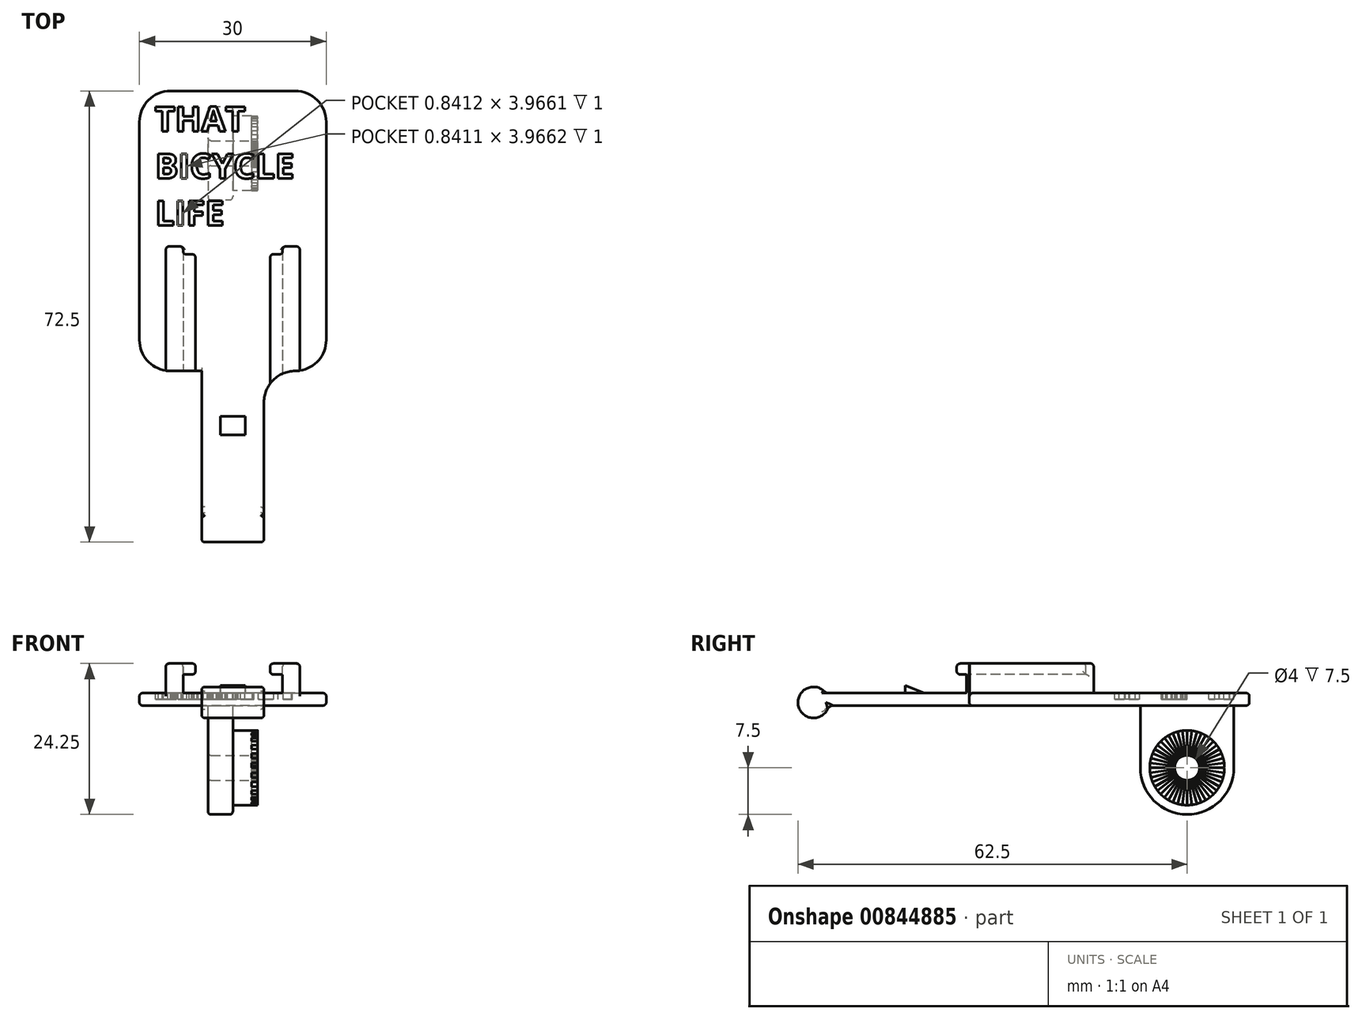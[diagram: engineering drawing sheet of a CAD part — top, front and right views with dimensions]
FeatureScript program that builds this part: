
annotation { "Feature Type Name" : "Feature", "Feature Type Description" : "" }
export const myFeature = defineFeature(function(context is Context, id is Id, definition is map)
    precondition{}
    {
        {
            var Q0;
            Q0=qCreatedBy(makeId("Top.planeOp"),FACE);
            var sketch = newSketch(context, id + "F0", { "sketchPlane" : qUnion([Q0])});
            skLineSegment(sketch, "E0.bottom", {"start": v(-15, 25) * mm, "end": v(15, 25) * mm});
            skLineSegment(sketch, "E0.top", {"start": v(-15, -20) * mm, "end": v(15, -20) * mm});
            skLineSegment(sketch, "E0.left", {"start": v(-15, 25) * mm, "end": v(-15, -20) * mm});
            skLineSegment(sketch, "E0.right", {"start": v(15, 25) * mm, "end": v(15, -20) * mm});
            skSolve(sketch);
        }
        {
            var Q0;
            Q0=qSketchRegion(id+"F0",true);
            extrude(context, id + "F1", {"entities" : qUnion([Q0]), "depth" : 2 * mm, "offsetDistance" : 25 * mm});
        }
        {
            var Q0;
            Q0=makeQuery(id+"F1.opExtrude","CAP_FACE",FACE,{"disambiguationData":[OSD([sQuery(id+"F0.wireOp",EDGE,"E0.bottom"),sQuery(id+"F0.wireOp",EDGE,"E0.top"),sQuery(id+"F0.wireOp",EDGE,"E0.left"),sQuery(id+"F0.wireOp",EDGE,"E0.right")])],"isStart":true});
            var sketch = newSketch(context, id + "F2", { "sketchPlane" : qUnion([Q0])});
            skLineSegment(sketch, "E1.bottom", {"start": v(10.75, 20) * mm, "end": v(-10.75, 20) * mm});
            skLineSegment(sketch, "E1.top", {"start": v(10.75, 0) * mm, "end": v(-10.75, 0) * mm});
            skLineSegment(sketch, "E1.left", {"start": v(10.75, 20) * mm, "end": v(10.75, 0) * mm});
            skLineSegment(sketch, "E1.right", {"start": v(-10.75, 20) * mm, "end": v(-10.75, 0) * mm});
            skSolve(sketch);
        }
        {
            var Q0;
            Q0=qSketchRegion(id+"F2",true);
            extrude(context, id + "F3", {"entities" : qUnion([Q0]), "operationType" : NewBodyOperationType.ADD, "depth" : 4.75 * mm, "offsetDistance" : 25 * mm});
        }
        {
            var Q0;
            Q0=makeQuery(id+"F3.boolean.opBoolean","MERGE",FACE,{"derivedFrom":[makeQuery(id+"FSz8aaNzwJ16Nas_1.boolean.opBoolean","MERGE",FACE,{"derivedFrom":[makeQuery(id+"F1.opExtrude","SWEPT_FACE",FACE,{"disambiguationData":[OSD([sQuery(id+"F0.wireOp",EDGE,"E0.top")])]}),makeQuery(id+"FSz8aaNzwJ16Nas_1.opExtrude","SWEPT_FACE",FACE,{"disambiguationData":[OSD([sQuery(id+"FtYRrhxxuHg0Pyv_1.wireOp",EDGE,"OmNEySeM-kDo9-KMJ4-0k0w-oykvhkZkCSKl.top")])]})]}),makeQuery(id+"F3.opExtrude","SWEPT_FACE",FACE,{"disambiguationData":[OSD([sQuery(id+"F2.wireOp",EDGE,"E1.bottom")])]})]});
            var sketch = newSketch(context, id + "F4", { "sketchPlane" : qUnion([Q0])});
            skLineSegment(sketch, "E2", {"start": v(-6, -4.75) * mm, "end": v(-6, -3) * mm});
            skLineSegment(sketch, "E3", {"start": v(-6, -3) * mm, "end": v(-8, -3) * mm});
            skLineSegment(sketch, "E4", {"start": v(-8, -3) * mm, "end": v(-8, 0) * mm});
            skLineSegment(sketch, "E5", {"start": v(-8, 0) * mm, "end": v(8, 0) * mm});
            skLineSegment(sketch, "E6", {"start": v(8, 0) * mm, "end": v(8, -3) * mm});
            skLineSegment(sketch, "E7", {"start": v(8, -3) * mm, "end": v(6, -3) * mm});
            skLineSegment(sketch, "E8", {"start": v(6, -3) * mm, "end": v(6, -4.75) * mm});
            skLineSegment(sketch, "E9", {"start": v(-6, -4.75) * mm, "end": v(6, -4.75) * mm});
            skSolve(sketch);
        }
        {
            var Q0;
            Q0=qSketchRegion(id+"F4",true);
            extrude(context, id + "F5", {"entities" : qUnion([Q0]), "operationType" : NewBodyOperationType.REMOVE, "oppositeDirection" : true, "depth" : 25 * mm, "offsetDistance" : 25 * mm});
        }
        {
            var Q0;
            Q0=qCreatedBy(makeId("Top.planeOp"),FACE);
            var sketch = newSketch(context, id + "F6", { "sketchPlane" : qUnion([Q0])});
            skLineSegment(sketch, "E10.bottom", {"start": v(5, -20) * mm, "end": v(-5, -20) * mm});
            skLineSegment(sketch, "E10.top", {"start": v(5, -45) * mm, "end": v(-5, -45) * mm});
            skLineSegment(sketch, "E10.left", {"start": v(5, -20) * mm, "end": v(5, -45) * mm});
            skLineSegment(sketch, "E10.right", {"start": v(-5, -20) * mm, "end": v(-5, -45) * mm});
            skSolve(sketch);
        }
        {
            var Q0;
            Q0=qSketchRegion(id+"F6",true);
            extrude(context, id + "F7", {"entities" : qUnion([Q0]), "operationType" : NewBodyOperationType.ADD, "depth" : 2 * mm, "offsetDistance" : 25 * mm});
        }
        {
            var Q0;
            Q0=qCreatedBy(makeId("Right.planeOp"),FACE);
            var sketch = newSketch(context, id + "F8", { "sketchPlane" : qUnion([Q0])});
            skLineSegment(sketch, "E11", {"start": v(-27.25, 0) * mm, "end": v(-30.25, -1.25) * mm});
            skLineSegment(sketch, "E12", {"start": v(-30.25, -1.25) * mm, "end": v(-30.25, 0) * mm});
            skLineSegment(sketch, "E13", {"start": v(-30.25, 0) * mm, "end": v(-27.25, 0) * mm});
            skSolve(sketch);
        }
        {
            var Q0;
            Q0=qSketchRegion(id+"F8",true);
            extrude(context, id + "F9", {"entities" : qUnion([Q0]), "operationType" : NewBodyOperationType.ADD, "endBound" : BoundingType.SYMMETRIC, "depth" : 4 * mm, "offsetDistance" : 25 * mm});
        }
        {
            var Q0;
            {var subQ0=sQuery(id+"F2.wireOp",EDGE,"E1.bottom");var subQ1=sQuery(id+"F2.wireOp",EDGE,"E1.top");var subQ2=sQuery(id+"F2.wireOp",EDGE,"E1.left");Q0=makeQuery(id+"F5.boolean.opBoolean","SPLIT",FACE,{"disambiguationData":[TD([makeQuery(id+"F3.opExtrude","SWEPT_FACE",FACE,{"disambiguationData":[OSD([subQ2])]})])],"derivedFrom":makeQuery(id+"F3.opExtrude","CAP_FACE",FACE,{"disambiguationData":[OSD([subQ0,subQ1,subQ2,sQuery(id+"F2.wireOp",EDGE,"E1.right")])],"isStart":false})});}
            var sketch = newSketch(context, id + "F10", { "sketchPlane" : qUnion([Q0])});
            skLineSegment(sketch, "E14.bottom", {"start": v(8, 1.25) * mm, "end": v(-8, 1.25) * mm});
            skLineSegment(sketch, "E14.top", {"start": v(8, -3.75) * mm, "end": v(-8, -3.75) * mm});
            skLineSegment(sketch, "E14.left", {"start": v(8, 1.25) * mm, "end": v(8, -3.75) * mm});
            skLineSegment(sketch, "E14.right", {"start": v(-8, 1.25) * mm, "end": v(-8, -3.75) * mm});
            skSolve(sketch);
        }
        {
            var Q0;
            Q0=qSketchRegion(id+"F10",true);
            extrude(context, id + "F11", {"entities" : qUnion([Q0]), "operationType" : NewBodyOperationType.REMOVE, "oppositeDirection" : true, "depth" : 4.75 * mm, "offsetDistance" : 25 * mm});
        }
        {
            var Q0;
            Q0=qCreatedBy(makeId("Right.planeOp"),FACE);
            var sketch = newSketch(context, id + "F12", { "sketchPlane" : qUnion([Q0])});
            skCircle(sketch, "E15", {"center": v(-45, 1.5) * mm, "radius": 2.5 * mm});
            skSolve(sketch);
        }
        {
            var Q0;
            Q0=qSketchRegion(id+"F12",true);
            extrude(context, id + "F13", {"entities" : qUnion([Q0]), "operationType" : NewBodyOperationType.ADD, "endBound" : BoundingType.SYMMETRIC, "depth" : 10 * mm, "offsetDistance" : 25 * mm});
        }
        {
            var Q0;
            Q0=qCreatedBy(makeId("Right.planeOp"),FACE);
            var sketch = newSketch(context, id + "F14", { "sketchPlane" : qUnion([Q0])});
            skLineSegment(sketch, "E16.0", {"start": v(22.5, 2) * mm, "end": v(7.5, 2) * mm});
            skArc(sketch, "E17", {"start": v(22.5, 12) * mm, "mid": v(15, 19.5) * mm, "end": v(7.5, 12) * mm});
            skLineSegment(sketch, "E18", {"start": v(22.5, 12) * mm, "end": v(22.5, 2) * mm});
            skLineSegment(sketch, "E19", {"start": v(7.5, 12) * mm, "end": v(7.5, 2) * mm});
            skPoint(sketch, "E20.orphan", {"position": v(25, 2) * mm});
            skSolve(sketch);
        }
        {
            var Q0;
            Q0 = qSketchRegion(id + "F14", true);
            extrude(context, id + "F15", {"entities" : qUnion([Q0]), "operationType" : NewBodyOperationType.ADD, "depth" : 4 * mm, "offsetDistance" : 25 * mm});
        }
        {
            var Q0;
            Q0=makeQuery(id+"F15.opExtrude","CAP_FACE",FACE,{"disambiguationData":[OSD([sQuery(id+"F14.wireOp",EDGE,"E16.0"),sQuery(id+"F14.wireOp",EDGE,"xAd6j7dT-fOeG-b4Lt-S26A-gevo38MO0Fub"),sQuery(id+"F14.wireOp",EDGE,"qkvuxE6E-48M7-aqLn-kGDS-jZh7hvvUHYrP"),sQuery(id+"F14.wireOp",EDGE,"y8K9iNXk-dUTU-x6BT-XT9c-BXyydat5kygA")])],"isStart":true});
            var sketch = newSketch(context, id + "F16", { "sketchPlane" : qUnion([Q0])});
            skCircle(sketch, "E21", {"center": v(-15, 12) * mm, "radius": 6 * mm});
            skSolve(sketch);
        }
        {
            var Q0;
            Q0 = qSketchRegion(id + "F16", true);
            extrude(context, id + "F17", {"entities" : qUnion([Q0]), "operationType" : NewBodyOperationType.ADD, "depth" : 4 * mm, "offsetDistance" : 25 * mm});
        }
        {
            var Q0;
            Q0=makeQuery(id+"F17.opExtrude","CAP_FACE",FACE,{"disambiguationData":[OSD([sQuery(id+"F16.wireOp",EDGE,"E21")])],"isStart":false});
            var sketch = newSketch(context, id + "F18", { "sketchPlane" : qUnion([Q0])});
            skArc(sketch, "E22", {"start": v(-20.95, 11.22) * mm, "mid": v(-20.88, 10.83) * mm, "end": v(-20.8, 10.45) * mm});
            skArc(sketch, "E23", {"start": v(-13.78, 10.41) * mm, "mid": v(-13.68, 10.5) * mm, "end": v(-13.59, 10.59) * mm});
            skLineSegment(sketch, "E24", {"start": v(-17, 12) * mm, "end": v(-21, 12) * mm});
            skLineSegment(sketch, "E25.1.0", {"start": v(-16.98, 11.74) * mm, "end": v(-20.95, 11.22) * mm});
            skLineSegment(sketch, "E25.2.0", {"start": v(-16.93, 11.48) * mm, "end": v(-20.8, 10.45) * mm});
            skLineSegment(sketch, "E25.3.0", {"start": v(-16.85, 11.23) * mm, "end": v(-20.54, 9.7) * mm});
            skLineSegment(sketch, "E25.4.0", {"start": v(-16.73, 11) * mm, "end": v(-20.2, 9) * mm});
            skLineSegment(sketch, "E25.5.0", {"start": v(-16.59, 10.78) * mm, "end": v(-19.76, 8.35) * mm});
            skLineSegment(sketch, "E25.6.0", {"start": v(-16.41, 10.59) * mm, "end": v(-19.24, 7.76) * mm});
            skLineSegment(sketch, "E25.7.0", {"start": v(-16.22, 10.41) * mm, "end": v(-18.65, 7.24) * mm});
            skLineSegment(sketch, "E25.8.0", {"start": v(-16, 10.27) * mm, "end": v(-18, 6.8) * mm});
            skLineSegment(sketch, "E25.9.0", {"start": v(-15.77, 10.15) * mm, "end": v(-17.3, 6.46) * mm});
            skLineSegment(sketch, "E25.10.0", {"start": v(-15.52, 10.07) * mm, "end": v(-16.55, 6.2) * mm});
            skLineSegment(sketch, "E25.11.0", {"start": v(-15.26, 10.02) * mm, "end": v(-15.78, 6.05) * mm});
            skLineSegment(sketch, "E25.12.0", {"start": v(-15, 10) * mm, "end": v(-15, 6) * mm});
            skLineSegment(sketch, "E25.13.0", {"start": v(-14.74, 10.02) * mm, "end": v(-14.22, 6.05) * mm});
            skLineSegment(sketch, "E25.14.0", {"start": v(-14.48, 10.07) * mm, "end": v(-13.45, 6.2) * mm});
            skLineSegment(sketch, "E25.15.0", {"start": v(-14.23, 10.15) * mm, "end": v(-12.7, 6.46) * mm});
            skLineSegment(sketch, "E25.16.0", {"start": v(-14, 10.27) * mm, "end": v(-12, 6.8) * mm});
            skLineSegment(sketch, "E25.17.0", {"start": v(-13.78, 10.41) * mm, "end": v(-11.35, 7.24) * mm});
            skLineSegment(sketch, "E25.18.0", {"start": v(-13.59, 10.59) * mm, "end": v(-10.76, 7.76) * mm});
            skLineSegment(sketch, "E25.19.0", {"start": v(-13.41, 10.78) * mm, "end": v(-10.24, 8.35) * mm});
            skLineSegment(sketch, "E25.20.0", {"start": v(-13.27, 11) * mm, "end": v(-9.8, 9) * mm});
            skLineSegment(sketch, "E25.21.0", {"start": v(-13.15, 11.23) * mm, "end": v(-9.46, 9.7) * mm});
            skLineSegment(sketch, "E25.22.0", {"start": v(-13.07, 11.48) * mm, "end": v(-9.2, 10.45) * mm});
            skLineSegment(sketch, "E25.23.0", {"start": v(-13.02, 11.74) * mm, "end": v(-9.05, 11.22) * mm});
            skLineSegment(sketch, "E25.24.0", {"start": v(-13, 12) * mm, "end": v(-9, 12) * mm});
            skLineSegment(sketch, "E25.25.0", {"start": v(-13.02, 12.26) * mm, "end": v(-9.05, 12.78) * mm});
            skLineSegment(sketch, "E25.26.0", {"start": v(-13.07, 12.52) * mm, "end": v(-9.2, 13.55) * mm});
            skLineSegment(sketch, "E25.27.0", {"start": v(-13.15, 12.77) * mm, "end": v(-9.46, 14.3) * mm});
            skLineSegment(sketch, "E25.28.0", {"start": v(-13.27, 13) * mm, "end": v(-9.8, 15) * mm});
            skLineSegment(sketch, "E25.29.0", {"start": v(-13.41, 13.22) * mm, "end": v(-10.24, 15.65) * mm});
            skLineSegment(sketch, "E25.30.0", {"start": v(-13.59, 13.41) * mm, "end": v(-10.76, 16.24) * mm});
            skLineSegment(sketch, "E25.31.0", {"start": v(-13.78, 13.59) * mm, "end": v(-11.35, 16.76) * mm});
            skLineSegment(sketch, "E25.32.0", {"start": v(-14, 13.73) * mm, "end": v(-12, 17.2) * mm});
            skLineSegment(sketch, "E25.33.0", {"start": v(-14.23, 13.85) * mm, "end": v(-12.7, 17.54) * mm});
            skLineSegment(sketch, "E25.34.0", {"start": v(-14.48, 13.93) * mm, "end": v(-13.45, 17.8) * mm});
            skLineSegment(sketch, "E25.35.0", {"start": v(-14.74, 13.98) * mm, "end": v(-14.22, 17.95) * mm});
            skLineSegment(sketch, "E25.36.0", {"start": v(-15, 14) * mm, "end": v(-15, 18) * mm});
            skLineSegment(sketch, "E25.37.0", {"start": v(-15.26, 13.98) * mm, "end": v(-15.78, 17.95) * mm});
            skLineSegment(sketch, "E25.38.0", {"start": v(-15.52, 13.93) * mm, "end": v(-16.55, 17.8) * mm});
            skLineSegment(sketch, "E25.39.0", {"start": v(-15.77, 13.85) * mm, "end": v(-17.3, 17.54) * mm});
            skLineSegment(sketch, "E25.40.0", {"start": v(-16, 13.73) * mm, "end": v(-18, 17.2) * mm});
            skLineSegment(sketch, "E25.41.0", {"start": v(-16.22, 13.59) * mm, "end": v(-18.65, 16.76) * mm});
            skLineSegment(sketch, "E25.42.0", {"start": v(-16.41, 13.41) * mm, "end": v(-19.24, 16.24) * mm});
            skLineSegment(sketch, "E25.43.0", {"start": v(-16.59, 13.22) * mm, "end": v(-19.76, 15.65) * mm});
            skLineSegment(sketch, "E25.44.0", {"start": v(-16.73, 13) * mm, "end": v(-20.2, 15) * mm});
            skLineSegment(sketch, "E25.45.0", {"start": v(-16.85, 12.77) * mm, "end": v(-20.54, 14.3) * mm});
            skLineSegment(sketch, "E25.46.0", {"start": v(-16.93, 12.52) * mm, "end": v(-20.8, 13.55) * mm});
            skLineSegment(sketch, "E25.47.0", {"start": v(-16.98, 12.26) * mm, "end": v(-20.95, 12.78) * mm});
            skArc(sketch, "E26.trimOffspring", {"start": v(-20.54, 9.7) * mm, "mid": v(-20.38, 9.35) * mm, "end": v(-20.2, 9) * mm});
            skArc(sketch, "E27.trimOffspring", {"start": v(-19.76, 8.35) * mm, "mid": v(-19.51, 8.04) * mm, "end": v(-19.24, 7.76) * mm});
            skArc(sketch, "E28.trimOffspring", {"start": v(-18.65, 7.24) * mm, "mid": v(-18.33, 7.01) * mm, "end": v(-18, 6.8) * mm});
            skArc(sketch, "E29.trimOffspring", {"start": v(-17.3, 6.46) * mm, "mid": v(-16.93, 6.32) * mm, "end": v(-16.55, 6.2) * mm});
            skArc(sketch, "E30.trimOffspring", {"start": v(-15.78, 6.05) * mm, "mid": v(-15.4, 6.01) * mm, "end": v(-15, 6) * mm});
            skArc(sketch, "E31.trimOffspring", {"start": v(-14.22, 6.05) * mm, "mid": v(-13.83, 6.12) * mm, "end": v(-13.45, 6.2) * mm});
            skArc(sketch, "E32.trimOffspring", {"start": v(-12.7, 6.46) * mm, "mid": v(-12.35, 6.62) * mm, "end": v(-12, 6.8) * mm});
            skArc(sketch, "E33.trimOffspring", {"start": v(-11.35, 7.24) * mm, "mid": v(-11.04, 7.49) * mm, "end": v(-10.76, 7.76) * mm});
            skArc(sketch, "E34.trimOffspring", {"start": v(-10.24, 8.35) * mm, "mid": v(-10.01, 8.67) * mm, "end": v(-9.8, 9) * mm});
            skArc(sketch, "E35.trimOffspring", {"start": v(-20.95, 12.78) * mm, "mid": v(-20.99, 12.4) * mm, "end": v(-21, 12) * mm});
            skArc(sketch, "E36.trimOffspring", {"start": v(-20.54, 14.3) * mm, "mid": v(-20.68, 13.93) * mm, "end": v(-20.8, 13.55) * mm});
            skArc(sketch, "E37.trimOffspring", {"start": v(-19.76, 15.65) * mm, "mid": v(-19.99, 15.33) * mm, "end": v(-20.2, 15) * mm});
            skArc(sketch, "E38.trimOffspring", {"start": v(-18.65, 16.76) * mm, "mid": v(-18.96, 16.51) * mm, "end": v(-19.24, 16.24) * mm});
            skArc(sketch, "E39.trimOffspring", {"start": v(-17.3, 17.54) * mm, "mid": v(-17.65, 17.38) * mm, "end": v(-18, 17.2) * mm});
            skArc(sketch, "E40.trimOffspring", {"start": v(-15.78, 17.95) * mm, "mid": v(-16.17, 17.88) * mm, "end": v(-16.55, 17.8) * mm});
            skArc(sketch, "E41.trimOffspring", {"start": v(-14.22, 17.95) * mm, "mid": v(-14.6, 17.99) * mm, "end": v(-15, 18) * mm});
            skArc(sketch, "E42.trimOffspring", {"start": v(-12.7, 17.54) * mm, "mid": v(-13.07, 17.68) * mm, "end": v(-13.45, 17.8) * mm});
            skArc(sketch, "E43.trimOffspring", {"start": v(-11.35, 16.76) * mm, "mid": v(-11.67, 16.99) * mm, "end": v(-12, 17.2) * mm});
            skArc(sketch, "E44.trimOffspring", {"start": v(-10.24, 15.65) * mm, "mid": v(-10.49, 15.96) * mm, "end": v(-10.76, 16.24) * mm});
            skArc(sketch, "E45.trimOffspring", {"start": v(-9.46, 14.3) * mm, "mid": v(-9.62, 14.65) * mm, "end": v(-9.8, 15) * mm});
            skArc(sketch, "E46.trimOffspring", {"start": v(-9.05, 12.78) * mm, "mid": v(-9.12, 13.17) * mm, "end": v(-9.2, 13.55) * mm});
            skArc(sketch, "E47.trimOffspring", {"start": v(-9.05, 11.22) * mm, "mid": v(-9.01, 11.6) * mm, "end": v(-9, 12) * mm});
            skArc(sketch, "E48.trimOffspring", {"start": v(-9.46, 9.7) * mm, "mid": v(-9.32, 10.07) * mm, "end": v(-9.2, 10.45) * mm});
            skArc(sketch, "E49.trimOffspring", {"start": v(-13.41, 10.78) * mm, "mid": v(-13.34, 10.89) * mm, "end": v(-13.27, 11) * mm});
            skArc(sketch, "E50.trimOffspring", {"start": v(-13.15, 11.23) * mm, "mid": v(-13.1, 11.36) * mm, "end": v(-13.07, 11.48) * mm});
            skArc(sketch, "E51.trimOffspring", {"start": v(-13.02, 11.74) * mm, "mid": v(-13, 11.87) * mm, "end": v(-13, 12) * mm});
            skArc(sketch, "E52.trimOffspring", {"start": v(-13.02, 12.26) * mm, "mid": v(-13.04, 12.4) * mm, "end": v(-13.07, 12.52) * mm});
            skArc(sketch, "E53.trimOffspring", {"start": v(-13.15, 12.77) * mm, "mid": v(-13.2, 12.88) * mm, "end": v(-13.27, 13) * mm});
            skArc(sketch, "E54.trimOffspring", {"start": v(-13.41, 13.22) * mm, "mid": v(-13.5, 13.32) * mm, "end": v(-13.59, 13.41) * mm});
            skArc(sketch, "E55.trimOffspring", {"start": v(-13.78, 13.59) * mm, "mid": v(-13.89, 13.66) * mm, "end": v(-14, 13.73) * mm});
            skArc(sketch, "E56.trimOffspring", {"start": v(-14.23, 13.85) * mm, "mid": v(-14.36, 13.9) * mm, "end": v(-14.48, 13.93) * mm});
            skArc(sketch, "E57.trimOffspring", {"start": v(-14.74, 13.98) * mm, "mid": v(-14.87, 14) * mm, "end": v(-15, 14) * mm});
            skArc(sketch, "E58.trimOffspring", {"start": v(-15.26, 13.98) * mm, "mid": v(-15.4, 13.96) * mm, "end": v(-15.52, 13.93) * mm});
            skArc(sketch, "E59.trimOffspring", {"start": v(-14.23, 10.15) * mm, "mid": v(-14.12, 10.2) * mm, "end": v(-14, 10.27) * mm});
            skArc(sketch, "E60.trimOffspring", {"start": v(-14.74, 10.02) * mm, "mid": v(-14.6, 10.04) * mm, "end": v(-14.48, 10.07) * mm});
            skArc(sketch, "E61.trimOffspring", {"start": v(-15.26, 10.02) * mm, "mid": v(-15.13, 10) * mm, "end": v(-15, 10) * mm});
            skArc(sketch, "E62.trimOffspring", {"start": v(-15.77, 10.15) * mm, "mid": v(-15.64, 10.1) * mm, "end": v(-15.52, 10.07) * mm});
            skArc(sketch, "E63.trimOffspring", {"start": v(-16.22, 10.41) * mm, "mid": v(-16.11, 10.34) * mm, "end": v(-16, 10.27) * mm});
            skArc(sketch, "E64.trimOffspring", {"start": v(-16.59, 10.78) * mm, "mid": v(-16.5, 10.68) * mm, "end": v(-16.41, 10.59) * mm});
            skArc(sketch, "E65.trimOffspring", {"start": v(-16.85, 11.23) * mm, "mid": v(-16.8, 11.12) * mm, "end": v(-16.73, 11) * mm});
            skArc(sketch, "E66.trimOffspring", {"start": v(-16.98, 11.74) * mm, "mid": v(-16.96, 11.6) * mm, "end": v(-16.93, 11.48) * mm});
            skArc(sketch, "E67.trimOffspring", {"start": v(-16.98, 12.26) * mm, "mid": v(-17, 12.13) * mm, "end": v(-17, 12) * mm});
            skArc(sketch, "E68.trimOffspring", {"start": v(-16.85, 12.77) * mm, "mid": v(-16.9, 12.64) * mm, "end": v(-16.93, 12.52) * mm});
            skArc(sketch, "E69.trimOffspring", {"start": v(-16.59, 13.22) * mm, "mid": v(-16.66, 13.11) * mm, "end": v(-16.73, 13) * mm});
            skArc(sketch, "E70.trimOffspring", {"start": v(-16.22, 13.59) * mm, "mid": v(-16.32, 13.5) * mm, "end": v(-16.41, 13.41) * mm});
            skArc(sketch, "E71.trimOffspring", {"start": v(-15.77, 13.85) * mm, "mid": v(-15.88, 13.8) * mm, "end": v(-16, 13.73) * mm});
            skSolve(sketch);
        }
        {
            var Q0;
            Q0=makeQuery(id+"F15.opExtrude","CAP_FACE",FACE,{"disambiguationData":[OSD([sQuery(id+"F14.wireOp",EDGE,"E16.0"),sQuery(id+"F14.wireOp",EDGE,"E17"),sQuery(id+"F14.wireOp",EDGE,"E18"),sQuery(id+"F14.wireOp",EDGE,"E19")])],"isStart":true});
            var sketch = newSketch(context, id + "F19", { "sketchPlane" : qUnion([Q0])});
            skCircle(sketch, "E72", {"center": v(-15, 12) * mm, "radius": 2 * mm});
            skSolve(sketch);
        }
        {
            var Q0;
            Q0 = qSketchRegion(id + "F19", true);
            extrude(context, id + "F20", {"entities" : qUnion([Q0]), "operationType" : NewBodyOperationType.REMOVE, "endBound" : BoundingType.SYMMETRIC, "oppositeDirection" : true, "depth" : 25 * mm, "offsetDistance" : 25 * mm});
        }
        {
            var Q0;
            Q0 = qSketchRegion(id + "F18", true);
            extrude(context, id + "F21", {"entities" : qUnion([Q0]), "operationType" : NewBodyOperationType.REMOVE, "oppositeDirection" : true, "depth" : 1 * mm, "offsetDistance" : 25 * mm});
        }
        {
            var Q0;
            Q0=makeQuery(id+"F1.opExtrude","SWEPT_EDGE",EDGE,{"disambiguationData":[OSD([sQuery(id+"F0.wireOp",EDGE,"E0.top"),sQuery(id+"F0.wireOp",EDGE,"E0.right")])]});
            var Q1;
            Q1=makeQuery(id+"F1.opExtrude","SWEPT_EDGE",EDGE,{"disambiguationData":[OSD([sQuery(id+"F0.wireOp",EDGE,"E0.top"),sQuery(id+"F0.wireOp",EDGE,"E0.left")])]});
            fillet(context, id + "F22", {"entities" : qUnion([Q0, Q1]), "radius" : 5 * mm, "tangentPropagation" : true, "allowEdgeOverflow" : false});
        }
        {
            var Q0;
            Q0=makeQuery(id+"F3.opExtrude","CAP_EDGE",EDGE,{"disambiguationData":[OSD([sQuery(id+"F2.wireOp",EDGE,"E1.left")])],"isStart":true});
            var Q1;
            Q1=makeQuery(id+"F3.opExtrude","CAP_EDGE",EDGE,{"disambiguationData":[OSD([sQuery(id+"F2.wireOp",EDGE,"E1.left")])],"isStart":false});
            var Q2;
            Q2=makeQuery(id+"F5.boolean.opBoolean","COPY",EDGE,{"derivedFrom":makeQuery(id+"F5.opExtrude","SWEPT_EDGE",EDGE,{"disambiguationData":[OSD([sQuery(id+"F2.wireOp",EDGE,"E1.bottom"),sQuery(id+"F4.wireOp",EDGE,"E8"),sQuery(id+"F4.wireOp",EDGE,"E9")])]})});
            var Q3;
            Q3=makeQuery(id+"F5.boolean.opBoolean","COPY",EDGE,{"derivedFrom":makeQuery(id+"F5.opExtrude","SWEPT_EDGE",EDGE,{"disambiguationData":[OSD([sQuery(id+"F4.wireOp",EDGE,"E7"),sQuery(id+"F4.wireOp",EDGE,"E8")])]})});
            var Q4;
            {var subQ0=sQuery(id+"F2.wireOp",EDGE,"E1.top");Q4=makeQuery(id+"F5.boolean.opBoolean","SPLIT",EDGE,{"disambiguationData":[TD([makeQuery(id+"F3.opExtrude","SWEPT_FACE",FACE,{"disambiguationData":[OSD([sQuery(id+"F2.wireOp",EDGE,"E1.left")])]})])],"derivedFrom":makeQuery(id+"F3.opExtrude","CAP_EDGE",EDGE,{"disambiguationData":[OSD([subQ0])],"isStart":true})});}
            var Q5;
            {var subQ0=sQuery(id+"F10.wireOp",EDGE,"E14.bottom");Q5=makeQuery(id+"F11.boolean.opBoolean","COPY",EDGE,{"disambiguationData":[TD([makeQuery(id+"F5.boolean.opBoolean","COPY",FACE,{"derivedFrom":makeQuery(id+"F5.opExtrude","SWEPT_FACE",FACE,{"disambiguationData":[OSD([sQuery(id+"F4.wireOp",EDGE,"E6")])]})})])],"derivedFrom":makeQuery(id+"F11.opExtrude","CAP_EDGE",EDGE,{"disambiguationData":[OSD([subQ0])],"isStart":true})});}
            var Q6;
            Q6=makeQuery(id+"F11.boolean.opBoolean","INTERSECT",EDGE,{"derivedFrom":[makeQuery(id+"F5.boolean.opBoolean","COPY",FACE,{"derivedFrom":makeQuery(id+"F5.opExtrude","SWEPT_FACE",FACE,{"disambiguationData":[OSD([sQuery(id+"F4.wireOp",EDGE,"E8")])]})}),makeQuery(id+"F11.opExtrude","SWEPT_FACE",FACE,{"disambiguationData":[OSD([sQuery(id+"F10.wireOp",EDGE,"E14.bottom")])]})]});
            var Q7;
            Q7=makeQuery(id+"F11.boolean.opBoolean","COPY",EDGE,{"derivedFrom":makeQuery(id+"F11.opExtrude","SWEPT_EDGE",EDGE,{"disambiguationData":[OSD([sQuery(id+"F10.wireOp",EDGE,"E14.bottom"),sQuery(id+"F10.wireOp",EDGE,"E14.left")])]})});
            var Q8;
            {var subQ0=sQuery(id+"F2.wireOp",EDGE,"E1.left");var subQ1=sQuery(id+"F2.wireOp",EDGE,"E1.top");Q8=makeQuery(id+"F5.boolean.opBoolean","SPLIT",EDGE,{"disambiguationData":[TD([makeQuery(id+"F3.opExtrude","SWEPT_FACE",FACE,{"disambiguationData":[OSD([subQ0])]})])],"derivedFrom":makeQuery(id+"F3.opExtrude","CAP_EDGE",EDGE,{"disambiguationData":[OSD([subQ1])],"isStart":false})});}
            fillet(context, id + "F23", {"entities" : qUnion([Q0, Q1, Q2, Q3, Q4, Q5, Q6, Q7, Q8]), "radius" : .5 * mm, "tangentPropagation" : true, "allowEdgeOverflow" : false});
        }
        {
            var Q0;
            Q0=makeQuery(id+"F3.opExtrude","CAP_EDGE",EDGE,{"disambiguationData":[OSD([sQuery(id+"F2.wireOp",EDGE,"E1.right")])],"isStart":false});
            var Q1;
            Q1=makeQuery(id+"F3.opExtrude","CAP_EDGE",EDGE,{"disambiguationData":[OSD([sQuery(id+"F2.wireOp",EDGE,"E1.right")])],"isStart":true});
            var Q2;
            {var subQ0=sQuery(id+"F2.wireOp",EDGE,"E1.top");Q2=makeQuery(id+"F5.boolean.opBoolean","SPLIT",EDGE,{"disambiguationData":[TD([makeQuery(id+"F3.opExtrude","SWEPT_FACE",FACE,{"disambiguationData":[OSD([sQuery(id+"F2.wireOp",EDGE,"E1.right")])]})])],"derivedFrom":makeQuery(id+"F3.opExtrude","CAP_EDGE",EDGE,{"disambiguationData":[OSD([subQ0])],"isStart":true})});}
            var Q3;
            {var subQ0=sQuery(id+"F2.wireOp",EDGE,"E1.right");var subQ1=sQuery(id+"F2.wireOp",EDGE,"E1.top");Q3=makeQuery(id+"F5.boolean.opBoolean","SPLIT",EDGE,{"disambiguationData":[TD([makeQuery(id+"F3.opExtrude","SWEPT_FACE",FACE,{"disambiguationData":[OSD([subQ0])]})])],"derivedFrom":makeQuery(id+"F3.opExtrude","CAP_EDGE",EDGE,{"disambiguationData":[OSD([subQ1])],"isStart":false})});}
            var Q4;
            {var subQ0=sQuery(id+"F10.wireOp",EDGE,"E14.bottom");Q4=makeQuery(id+"F11.boolean.opBoolean","COPY",EDGE,{"disambiguationData":[TD([makeQuery(id+"F5.boolean.opBoolean","COPY",FACE,{"derivedFrom":makeQuery(id+"F5.opExtrude","SWEPT_FACE",FACE,{"disambiguationData":[OSD([sQuery(id+"F4.wireOp",EDGE,"E2")])]})})])],"derivedFrom":makeQuery(id+"F11.opExtrude","CAP_EDGE",EDGE,{"disambiguationData":[OSD([subQ0])],"isStart":true})});}
            var Q5;
            Q5=makeQuery(id+"F11.boolean.opBoolean","COPY",EDGE,{"derivedFrom":makeQuery(id+"F11.opExtrude","SWEPT_EDGE",EDGE,{"disambiguationData":[OSD([sQuery(id+"F10.wireOp",EDGE,"E14.bottom"),sQuery(id+"F10.wireOp",EDGE,"E14.right")])]})});
            var Q6;
            Q6=makeQuery(id+"F11.boolean.opBoolean","INTERSECT",EDGE,{"derivedFrom":[makeQuery(id+"F5.boolean.opBoolean","COPY",FACE,{"derivedFrom":makeQuery(id+"F5.opExtrude","SWEPT_FACE",FACE,{"disambiguationData":[OSD([sQuery(id+"F4.wireOp",EDGE,"E2")])]})}),makeQuery(id+"F11.opExtrude","SWEPT_FACE",FACE,{"disambiguationData":[OSD([sQuery(id+"F10.wireOp",EDGE,"E14.bottom")])]})]});
            var Q7;
            Q7=makeQuery(id+"F5.boolean.opBoolean","COPY",EDGE,{"derivedFrom":makeQuery(id+"F5.opExtrude","SWEPT_EDGE",EDGE,{"disambiguationData":[OSD([sQuery(id+"F4.wireOp",EDGE,"E2"),sQuery(id+"F4.wireOp",EDGE,"E3")])]})});
            var Q8;
            Q8=makeQuery(id+"F5.boolean.opBoolean","COPY",EDGE,{"derivedFrom":makeQuery(id+"F5.opExtrude","SWEPT_EDGE",EDGE,{"disambiguationData":[OSD([sQuery(id+"F2.wireOp",EDGE,"E1.bottom"),sQuery(id+"F4.wireOp",EDGE,"E2"),sQuery(id+"F4.wireOp",EDGE,"E9")])]})});
            fillet(context, id + "F24", {"entities" : qUnion([Q0, Q1, Q2, Q3, Q4, Q5, Q6, Q7, Q8]), "radius" : .5 * mm, "tangentPropagation" : true, "allowEdgeOverflow" : false});
        }
        {
            var Q0;
            Q0=makeQuery(id+"F5.boolean.opBoolean","COPY",EDGE,{"derivedFrom":makeQuery(id+"F5.opExtrude","SWEPT_EDGE",EDGE,{"disambiguationData":[OSD([sQuery(id+"F4.wireOp",EDGE,"E5"),sQuery(id+"F4.wireOp",EDGE,"E6")])]})});
            var Q1;
            Q1=makeQuery(id+"F5.boolean.opBoolean","COPY",EDGE,{"derivedFrom":makeQuery(id+"F5.opExtrude","SWEPT_EDGE",EDGE,{"disambiguationData":[OSD([sQuery(id+"F4.wireOp",EDGE,"E4"),sQuery(id+"F4.wireOp",EDGE,"E5")])]})});
            var Q2;
            Q2=makeQuery(id+"F5.boolean.opBoolean","COPY",EDGE,{"derivedFrom":makeQuery(id+"F5.opExtrude","SWEPT_EDGE",EDGE,{"disambiguationData":[OSD([sQuery(id+"F4.wireOp",EDGE,"E3"),sQuery(id+"F4.wireOp",EDGE,"E4")])]})});
            var Q3;
            Q3=makeQuery(id+"F5.boolean.opBoolean","COPY",EDGE,{"derivedFrom":makeQuery(id+"F5.opExtrude","SWEPT_EDGE",EDGE,{"disambiguationData":[OSD([sQuery(id+"F4.wireOp",EDGE,"E6"),sQuery(id+"F4.wireOp",EDGE,"E7")])]})});
            fillet(context, id + "F25", {"entities" : qUnion([Q0, Q1, Q2, Q3]), "radius" : 0.25 * mm, "tangentPropagation" : true, "allowEdgeOverflow" : false});
        }
        {
            var Q0;
            Q0=makeQuery(id+"F3.opExtrude","SWEPT_EDGE",EDGE,{"disambiguationData":[OSD([sQuery(id+"F2.wireOp",EDGE,"E1.top"),sQuery(id+"F2.wireOp",EDGE,"E1.right")])]});
            var Q1;
            {var subQ0=sQuery(id+"F2.wireOp",EDGE,"E1.left");var subQ1=sQuery(id+"F2.wireOp",EDGE,"E1.top");Q1=makeQuery(id+"F11.boolean.opBoolean","INTERSECT",EDGE,{"derivedFrom":[makeQuery(id+"F5.boolean.opBoolean","SPLIT",FACE,{"disambiguationData":[TD([makeQuery(id+"F3.opExtrude","SWEPT_FACE",FACE,{"disambiguationData":[OSD([subQ0])]})])],"derivedFrom":makeQuery(id+"F3.opExtrude","SWEPT_FACE",FACE,{"disambiguationData":[OSD([subQ1])]})}),makeQuery(id+"F11.opExtrude","SWEPT_FACE",FACE,{"disambiguationData":[OSD([sQuery(id+"F10.wireOp",EDGE,"E14.left")])]})]});}
            var Q2;
            Q2=makeQuery(id+"F3.opExtrude","SWEPT_EDGE",EDGE,{"disambiguationData":[OSD([sQuery(id+"F2.wireOp",EDGE,"E1.top"),sQuery(id+"F2.wireOp",EDGE,"E1.left")])]});
            var Q3;
            {var subQ0=sQuery(id+"F2.wireOp",EDGE,"E1.right");var subQ1=sQuery(id+"F2.wireOp",EDGE,"E1.top");Q3=makeQuery(id+"F11.boolean.opBoolean","INTERSECT",EDGE,{"derivedFrom":[makeQuery(id+"F5.boolean.opBoolean","SPLIT",FACE,{"disambiguationData":[TD([makeQuery(id+"F3.opExtrude","SWEPT_FACE",FACE,{"disambiguationData":[OSD([subQ0])]})])],"derivedFrom":makeQuery(id+"F3.opExtrude","SWEPT_FACE",FACE,{"disambiguationData":[OSD([subQ1])]})}),makeQuery(id+"F11.opExtrude","SWEPT_FACE",FACE,{"disambiguationData":[OSD([sQuery(id+"F10.wireOp",EDGE,"E14.right")])]})]});}
            fillet(context, id + "F26", {"entities" : qUnion([Q0, Q1, Q2, Q3]), "radius" : .5 * mm, "tangentPropagation" : true, "allowEdgeOverflow" : false});
        }
        {
            var Q0;
            Q0=makeQuery(id+"F7.opExtrude","SWEPT_EDGE",EDGE,{"disambiguationData":[OSD([sQuery(id+"F6.wireOp",EDGE,"E10.bottom"),sQuery(id+"F6.wireOp",EDGE,"E10.left")])]});
            var Q1;
            Q1=makeQuery(id+"F7.opExtrude","SWEPT_EDGE",EDGE,{"disambiguationData":[OSD([sQuery(id+"F6.wireOp",EDGE,"E10.bottom"),sQuery(id+"F6.wireOp",EDGE,"E10.right")])]});
            fillet(context, id + "F27", {"entities" : qUnion([Q0, Q1]), "radius" : 5 * mm, "tangentPropagation" : true, "allowEdgeOverflow" : false});
        }
        {
            var Q0;
            Q0=qCreatedBy(makeId("Top.planeOp"),FACE);
            var sketch = newSketch(context, id + "F28", { "sketchPlane" : qUnion([Q0])});
            skLineSegment(sketch, "E73", {"start": v(0, 47.57) * mm, "end": v(0, -65.1) * mm});
            skSolve(sketch);
        }
        {
            var Q0;
            Q0=makeQuery(id+"F1.opExtrude","SWEPT_BODY",BODY,{"disambiguationData":[OSD([sQuery(id+"F0.wireOp",EDGE,"E0.bottom"),sQuery(id+"F0.wireOp",EDGE,"E0.top"),sQuery(id+"F0.wireOp",EDGE,"E0.left"),sQuery(id+"F0.wireOp",EDGE,"E0.right")])]});
            var Q1;
            Q1=sQuery(id+"F28.wireOp",EDGE,"E73");
            var Q2;
            Q2=sQuery(id+"F28.wireOp",EDGE,"E73");
            transform(context, id + "F29", {"entities" : qUnion([Q0]), "transformType" : TransformType.ROTATION, "transformAxis" : qUnion([Q2]), "angle" : 180 * degree, "makeCopy" : false});
        }
        {
            var Q0;
            Q0=makeQuery(id+"F7.boolean.opBoolean","MERGE",FACE,{"derivedFrom":[makeQuery(id+"F5.boolean.opBoolean","MERGE",FACE,{"derivedFrom":[makeQuery(id+"F1.opExtrude","CAP_FACE",FACE,{"disambiguationData":[OSD([sQuery(id+"F0.wireOp",EDGE,"E0.bottom"),sQuery(id+"F0.wireOp",EDGE,"E0.top"),sQuery(id+"F0.wireOp",EDGE,"E0.left"),sQuery(id+"F0.wireOp",EDGE,"E0.right")])],"isStart":true}),makeQuery(id+"F5.opExtrude","SWEPT_FACE",FACE,{"disambiguationData":[OSD([sQuery(id+"F4.wireOp",EDGE,"E5")])]})]}),makeQuery(id+"F7.opExtrude","CAP_FACE",FACE,{"disambiguationData":[OSD([sQuery(id+"F6.wireOp",EDGE,"E10.bottom"),sQuery(id+"F6.wireOp",EDGE,"E10.top"),sQuery(id+"F6.wireOp",EDGE,"E10.left"),sQuery(id+"F6.wireOp",EDGE,"E10.right")])],"isStart":true})]});
            var sketch = newSketch(context, id + "F30", { "sketchPlane" : qUnion([Q0])});
            skText(sketch, "E74", { "text": "THAT\nBICYCLE\nLIFE", "fontName": "OpenSans-Bold.ttf"});
            const initialGuessF30  = {"E74": [-0.0125, 0.0185, 1, 0, 0.004]};
            skSetInitialGuess(sketch, initialGuessF30);
            skSolve(sketch);
        }
        {
            var Q0;
            Q0=qSketchRegion(id+"F30",true);
            extrude(context, id + "F31", {"entities" : qUnion([Q0]), "operationType" : NewBodyOperationType.REMOVE, "oppositeDirection" : true, "depth" : 1 * mm, "offsetDistance" : 25 * mm});
        }
        {
            var Q0;
            Q0=makeQuery(id+"F1.opExtrude","SWEPT_EDGE",EDGE,{"disambiguationData":[OSD([sQuery(id+"F0.wireOp",EDGE,"E0.bottom"),sQuery(id+"F0.wireOp",EDGE,"E0.left")])]});
            var Q1;
            Q1=makeQuery(id+"F1.opExtrude","SWEPT_EDGE",EDGE,{"disambiguationData":[OSD([sQuery(id+"F0.wireOp",EDGE,"E0.bottom"),sQuery(id+"F0.wireOp",EDGE,"E0.right")])]});
            fillet(context, id + "F32", {"entities" : qUnion([Q0, Q1]), "radius" : 5 * mm, "tangentPropagation" : true, "allowEdgeOverflow" : false});
        }
        {
            var Q0;
            Q0=makeQuery(id+"F1.opExtrude","CAP_EDGE",EDGE,{"disambiguationData":[OSD([sQuery(id+"F0.wireOp",EDGE,"E0.right")])],"isStart":false});
            var Q1;
            Q1=makeQuery(id+"F1.opExtrude","CAP_EDGE",EDGE,{"disambiguationData":[OSD([sQuery(id+"F0.wireOp",EDGE,"E0.right")])],"isStart":true});
            var Q2;
            {var subQ0=sQuery(id+"F6.wireOp",EDGE,"E10.left");var subQ1=sQuery(id+"F6.wireOp",EDGE,"E10.bottom");Q2=makeQuery(id+"F27.opFillet","BLEND_EDGE",EDGE,{"blendedFrom":[makeQuery(id+"F7.opExtrude","SWEPT_EDGE",EDGE,{"disambiguationData":[OSD([subQ1,subQ0])]}),makeQuery(id+"F7.opExtrude","CAP_FACE",FACE,{"disambiguationData":[OSD([subQ1,sQuery(id+"F6.wireOp",EDGE,"E10.top"),subQ0,sQuery(id+"F6.wireOp",EDGE,"E10.right")])],"isStart":false})],"blendedInto":[makeQuery(id+"F7.opExtrude","CAP_FACE",FACE,{"disambiguationData":[OSD([subQ1,sQuery(id+"F6.wireOp",EDGE,"E10.top"),subQ0,sQuery(id+"F6.wireOp",EDGE,"E10.right")])],"isStart":false})]});}
            var Q3;
            {var subQ0=sQuery(id+"F6.wireOp",EDGE,"E10.right");var subQ1=sQuery(id+"F6.wireOp",EDGE,"E10.bottom");Q3=makeQuery(id+"F27.opFillet","BLEND_EDGE",EDGE,{"blendedFrom":[makeQuery(id+"F7.opExtrude","SWEPT_EDGE",EDGE,{"disambiguationData":[OSD([subQ1,subQ0])]}),makeQuery(id+"F7.opExtrude","CAP_FACE",FACE,{"disambiguationData":[OSD([subQ1,sQuery(id+"F6.wireOp",EDGE,"E10.top"),sQuery(id+"F6.wireOp",EDGE,"E10.left"),subQ0])],"isStart":false})],"blendedInto":[makeQuery(id+"F7.opExtrude","CAP_FACE",FACE,{"disambiguationData":[OSD([subQ1,sQuery(id+"F6.wireOp",EDGE,"E10.top"),sQuery(id+"F6.wireOp",EDGE,"E10.left"),subQ0])],"isStart":false})]});}
            var Q4;
            Q4=makeQuery(id+"F13.opExtrude","CAP_EDGE",EDGE,{"disambiguationData":[OSD([sQuery(id+"F12.wireOp",EDGE,"E15")])],"isStart":true});
            var Q5;
            Q5=makeQuery(id+"F13.opExtrude","CAP_EDGE",EDGE,{"disambiguationData":[OSD([sQuery(id+"F12.wireOp",EDGE,"E15")])],"isStart":false});
            fillet(context, id + "F33", {"entities" : qUnion([Q0, Q1, Q2, Q3, Q4, Q5]), "radius" : .5 * mm, "tangentPropagation" : true, "allowEdgeOverflow" : false});
        }
        {
            var Q0;
            Q0=makeQuery(id+"F13.boolean.opBoolean","INTERSECT",EDGE,{"derivedFrom":[makeQuery(id+"F7.opExtrude","CAP_FACE",FACE,{"disambiguationData":[OSD([sQuery(id+"F6.wireOp",EDGE,"E10.bottom"),sQuery(id+"F6.wireOp",EDGE,"E10.top"),sQuery(id+"F6.wireOp",EDGE,"E10.left"),sQuery(id+"F6.wireOp",EDGE,"E10.right")])],"isStart":false}),makeQuery(id+"F13.opExtrude","SWEPT_FACE",FACE,{"disambiguationData":[OSD([sQuery(id+"F12.wireOp",EDGE,"E15")])]})]});
            var Q1;
            Q1=makeQuery(id+"F13.boolean.opBoolean","INTERSECT",EDGE,{"derivedFrom":[makeQuery(id+"F7.boolean.opBoolean","MERGE",FACE,{"derivedFrom":[makeQuery(id+"F5.boolean.opBoolean","MERGE",FACE,{"derivedFrom":[makeQuery(id+"F1.opExtrude","CAP_FACE",FACE,{"disambiguationData":[OSD([sQuery(id+"F0.wireOp",EDGE,"E0.bottom"),sQuery(id+"F0.wireOp",EDGE,"E0.top"),sQuery(id+"F0.wireOp",EDGE,"E0.left"),sQuery(id+"F0.wireOp",EDGE,"E0.right")])],"isStart":true}),makeQuery(id+"F5.opExtrude","SWEPT_FACE",FACE,{"disambiguationData":[OSD([sQuery(id+"F4.wireOp",EDGE,"E5")])]})]}),makeQuery(id+"F7.opExtrude","CAP_FACE",FACE,{"disambiguationData":[OSD([sQuery(id+"F6.wireOp",EDGE,"E10.bottom"),sQuery(id+"F6.wireOp",EDGE,"E10.top"),sQuery(id+"F6.wireOp",EDGE,"E10.left"),sQuery(id+"F6.wireOp",EDGE,"E10.right")])],"isStart":true})]}),makeQuery(id+"F13.opExtrude","SWEPT_FACE",FACE,{"disambiguationData":[OSD([sQuery(id+"F12.wireOp",EDGE,"E15")])]})]});
            fillet(context, id + "F34", {"entities" : qUnion([Q0, Q1]), "radius" : 1 * mm, "tangentPropagation" : true, "allowEdgeOverflow" : false});
        }
        {
            var Q0;
            Q0=makeQuery(id+"F15.opExtrude","CAP_EDGE",EDGE,{"disambiguationData":[OSD([sQuery(id+"F14.wireOp",EDGE,"E16.0")])],"isStart":true});
            var Q1;
            Q1=makeQuery(id+"F15.opExtrude","CAP_EDGE",EDGE,{"disambiguationData":[OSD([sQuery(id+"F14.wireOp",EDGE,"E17")])],"isStart":true});
            var Q2;
            Q2=makeQuery(id+"F15.opExtrude","CAP_EDGE",EDGE,{"disambiguationData":[OSD([sQuery(id+"F14.wireOp",EDGE,"E17")])],"isStart":false});
            var Q3;
            Q3=makeQuery(id+"F20.boolean.opBoolean","INTERSECT",EDGE,{"derivedFrom":[makeQuery(id+"F15.opExtrude","CAP_FACE",FACE,{"disambiguationData":[OSD([sQuery(id+"F14.wireOp",EDGE,"E16.0"),sQuery(id+"F14.wireOp",EDGE,"E17"),sQuery(id+"F14.wireOp",EDGE,"E18"),sQuery(id+"F14.wireOp",EDGE,"E19")])],"isStart":false}),makeQuery(id+"F20.opExtrude","SWEPT_FACE",FACE,{"disambiguationData":[OSD([sQuery(id+"F19.wireOp",EDGE,"E72")])]})]});
            var Q4;
            {var subQ0=makeQuery(id+"F17.opExtrude","CAP_FACE",FACE,{"disambiguationData":[OSD([sQuery(id+"F16.wireOp",EDGE,"E21")])],"isStart":false});var subQ1=makeQuery(id+"F20.opExtrude","SWEPT_FACE",FACE,{"disambiguationData":[OSD([sQuery(id+"F19.wireOp",EDGE,"E72")])]});Q4=makeQuery(id+"F21.boolean.opBoolean","SPLIT",EDGE,{"disambiguationData":[TD([makeQuery(id+"F21.opExtrude","SWEPT_FACE",FACE,{"disambiguationData":[OSD([sQuery(id+"F18.wireOp",EDGE,"30cf533b-c859-4f95-b794-18c5afbc5071.27.0")])]})])],"derivedFrom":makeQuery(id+"F20.boolean.opBoolean","INTERSECT",EDGE,{"derivedFrom":[subQ0,subQ1]})});}
            var Q5;
            {var subQ0=makeQuery(id+"F17.opExtrude","CAP_FACE",FACE,{"disambiguationData":[OSD([sQuery(id+"F16.wireOp",EDGE,"E21")])],"isStart":false});var subQ1=makeQuery(id+"F20.opExtrude","SWEPT_FACE",FACE,{"disambiguationData":[OSD([sQuery(id+"F19.wireOp",EDGE,"E72")])]});Q5=makeQuery(id+"F21.boolean.opBoolean","SPLIT",EDGE,{"disambiguationData":[TD([makeQuery(id+"F21.opExtrude","SWEPT_FACE",FACE,{"disambiguationData":[OSD([sQuery(id+"F18.wireOp",EDGE,"30cf533b-c859-4f95-b794-18c5afbc5071.29.0")])]})])],"derivedFrom":makeQuery(id+"F20.boolean.opBoolean","INTERSECT",EDGE,{"derivedFrom":[subQ0,subQ1]})});}
            var Q6;
            {var subQ0=makeQuery(id+"F17.opExtrude","CAP_FACE",FACE,{"disambiguationData":[OSD([sQuery(id+"F16.wireOp",EDGE,"E21")])],"isStart":false});var subQ1=makeQuery(id+"F20.opExtrude","SWEPT_FACE",FACE,{"disambiguationData":[OSD([sQuery(id+"F19.wireOp",EDGE,"E72")])]});Q6=makeQuery(id+"F21.boolean.opBoolean","SPLIT",EDGE,{"disambiguationData":[TD([makeQuery(id+"F21.opExtrude","SWEPT_FACE",FACE,{"disambiguationData":[OSD([sQuery(id+"F18.wireOp",EDGE,"30cf533b-c859-4f95-b794-18c5afbc5071.31.0")])]})])],"derivedFrom":makeQuery(id+"F20.boolean.opBoolean","INTERSECT",EDGE,{"derivedFrom":[subQ0,subQ1]})});}
            var Q7;
            {var subQ0=makeQuery(id+"F17.opExtrude","CAP_FACE",FACE,{"disambiguationData":[OSD([sQuery(id+"F16.wireOp",EDGE,"E21")])],"isStart":false});var subQ1=makeQuery(id+"F20.opExtrude","SWEPT_FACE",FACE,{"disambiguationData":[OSD([sQuery(id+"F19.wireOp",EDGE,"E72")])]});Q7=makeQuery(id+"F21.boolean.opBoolean","SPLIT",EDGE,{"disambiguationData":[TD([makeQuery(id+"F21.opExtrude","SWEPT_FACE",FACE,{"disambiguationData":[OSD([sQuery(id+"F18.wireOp",EDGE,"30cf533b-c859-4f95-b794-18c5afbc5071.25.0")])]})])],"derivedFrom":makeQuery(id+"F20.boolean.opBoolean","INTERSECT",EDGE,{"derivedFrom":[subQ0,subQ1]})});}
            var Q8;
            {var subQ0=makeQuery(id+"F17.opExtrude","CAP_FACE",FACE,{"disambiguationData":[OSD([sQuery(id+"F16.wireOp",EDGE,"E21")])],"isStart":false});var subQ1=makeQuery(id+"F20.opExtrude","SWEPT_FACE",FACE,{"disambiguationData":[OSD([sQuery(id+"F19.wireOp",EDGE,"E72")])]});Q8=makeQuery(id+"F21.boolean.opBoolean","SPLIT",EDGE,{"disambiguationData":[TD([makeQuery(id+"F21.opExtrude","SWEPT_FACE",FACE,{"disambiguationData":[OSD([sQuery(id+"F18.wireOp",EDGE,"30cf533b-c859-4f95-b794-18c5afbc5071.23.0")])]})])],"derivedFrom":makeQuery(id+"F20.boolean.opBoolean","INTERSECT",EDGE,{"derivedFrom":[subQ0,subQ1]})});}
            var Q9;
            {var subQ0=makeQuery(id+"F17.opExtrude","CAP_FACE",FACE,{"disambiguationData":[OSD([sQuery(id+"F16.wireOp",EDGE,"E21")])],"isStart":false});var subQ1=makeQuery(id+"F20.opExtrude","SWEPT_FACE",FACE,{"disambiguationData":[OSD([sQuery(id+"F19.wireOp",EDGE,"E72")])]});Q9=makeQuery(id+"F21.boolean.opBoolean","SPLIT",EDGE,{"disambiguationData":[TD([makeQuery(id+"F21.opExtrude","SWEPT_FACE",FACE,{"disambiguationData":[OSD([sQuery(id+"F18.wireOp",EDGE,"30cf533b-c859-4f95-b794-18c5afbc5071.21.0")])]})])],"derivedFrom":makeQuery(id+"F20.boolean.opBoolean","INTERSECT",EDGE,{"derivedFrom":[subQ0,subQ1]})});}
            var Q10;
            {var subQ0=makeQuery(id+"F17.opExtrude","CAP_FACE",FACE,{"disambiguationData":[OSD([sQuery(id+"F16.wireOp",EDGE,"E21")])],"isStart":false});var subQ1=makeQuery(id+"F20.opExtrude","SWEPT_FACE",FACE,{"disambiguationData":[OSD([sQuery(id+"F19.wireOp",EDGE,"E72")])]});Q10=makeQuery(id+"F21.boolean.opBoolean","SPLIT",EDGE,{"disambiguationData":[TD([makeQuery(id+"F21.opExtrude","SWEPT_FACE",FACE,{"disambiguationData":[OSD([sQuery(id+"F18.wireOp",EDGE,"30cf533b-c859-4f95-b794-18c5afbc5071.19.0")])]})])],"derivedFrom":makeQuery(id+"F20.boolean.opBoolean","INTERSECT",EDGE,{"derivedFrom":[subQ0,subQ1]})});}
            var Q11;
            {var subQ0=makeQuery(id+"F17.opExtrude","CAP_FACE",FACE,{"disambiguationData":[OSD([sQuery(id+"F16.wireOp",EDGE,"E21")])],"isStart":false});var subQ1=makeQuery(id+"F20.opExtrude","SWEPT_FACE",FACE,{"disambiguationData":[OSD([sQuery(id+"F19.wireOp",EDGE,"E72")])]});Q11=makeQuery(id+"F21.boolean.opBoolean","SPLIT",EDGE,{"disambiguationData":[TD([makeQuery(id+"F21.opExtrude","SWEPT_FACE",FACE,{"disambiguationData":[OSD([sQuery(id+"F18.wireOp",EDGE,"30cf533b-c859-4f95-b794-18c5afbc5071.17.0")])]})])],"derivedFrom":makeQuery(id+"F20.boolean.opBoolean","INTERSECT",EDGE,{"derivedFrom":[subQ0,subQ1]})});}
            var Q12;
            {var subQ0=makeQuery(id+"F17.opExtrude","CAP_FACE",FACE,{"disambiguationData":[OSD([sQuery(id+"F16.wireOp",EDGE,"E21")])],"isStart":false});var subQ1=makeQuery(id+"F20.opExtrude","SWEPT_FACE",FACE,{"disambiguationData":[OSD([sQuery(id+"F19.wireOp",EDGE,"E72")])]});Q12=makeQuery(id+"F21.boolean.opBoolean","SPLIT",EDGE,{"disambiguationData":[TD([makeQuery(id+"F21.opExtrude","SWEPT_FACE",FACE,{"disambiguationData":[OSD([sQuery(id+"F18.wireOp",EDGE,"30cf533b-c859-4f95-b794-18c5afbc5071.33.0")])]})])],"derivedFrom":makeQuery(id+"F20.boolean.opBoolean","INTERSECT",EDGE,{"derivedFrom":[subQ0,subQ1]})});}
            var Q13;
            {var subQ0=makeQuery(id+"F17.opExtrude","CAP_FACE",FACE,{"disambiguationData":[OSD([sQuery(id+"F16.wireOp",EDGE,"E21")])],"isStart":false});var subQ1=makeQuery(id+"F20.opExtrude","SWEPT_FACE",FACE,{"disambiguationData":[OSD([sQuery(id+"F19.wireOp",EDGE,"E72")])]});Q13=makeQuery(id+"F21.boolean.opBoolean","SPLIT",EDGE,{"disambiguationData":[TD([makeQuery(id+"F21.opExtrude","SWEPT_FACE",FACE,{"disambiguationData":[OSD([sQuery(id+"F18.wireOp",EDGE,"30cf533b-c859-4f95-b794-18c5afbc5071.35.0")])]})])],"derivedFrom":makeQuery(id+"F20.boolean.opBoolean","INTERSECT",EDGE,{"derivedFrom":[subQ0,subQ1]})});}
            var Q14;
            {var subQ0=makeQuery(id+"F17.opExtrude","CAP_FACE",FACE,{"disambiguationData":[OSD([sQuery(id+"F16.wireOp",EDGE,"E21")])],"isStart":false});var subQ1=makeQuery(id+"F20.opExtrude","SWEPT_FACE",FACE,{"disambiguationData":[OSD([sQuery(id+"F19.wireOp",EDGE,"E72")])]});Q14=makeQuery(id+"F21.boolean.opBoolean","SPLIT",EDGE,{"disambiguationData":[TD([makeQuery(id+"F21.opExtrude","SWEPT_FACE",FACE,{"disambiguationData":[OSD([sQuery(id+"F18.wireOp",EDGE,"30cf533b-c859-4f95-b794-18c5afbc5071.37.0")])]})])],"derivedFrom":makeQuery(id+"F20.boolean.opBoolean","INTERSECT",EDGE,{"derivedFrom":[subQ0,subQ1]})});}
            var Q15;
            {var subQ0=makeQuery(id+"F17.opExtrude","CAP_FACE",FACE,{"disambiguationData":[OSD([sQuery(id+"F16.wireOp",EDGE,"E21")])],"isStart":false});var subQ1=makeQuery(id+"F20.opExtrude","SWEPT_FACE",FACE,{"disambiguationData":[OSD([sQuery(id+"F19.wireOp",EDGE,"E72")])]});Q15=makeQuery(id+"F21.boolean.opBoolean","SPLIT",EDGE,{"disambiguationData":[TD([makeQuery(id+"F21.opExtrude","SWEPT_FACE",FACE,{"disambiguationData":[OSD([sQuery(id+"F18.wireOp",EDGE,"30cf533b-c859-4f95-b794-18c5afbc5071.5.0")])]})])],"derivedFrom":makeQuery(id+"F20.boolean.opBoolean","INTERSECT",EDGE,{"derivedFrom":[subQ0,subQ1]})});}
            var Q16;
            {var subQ0=makeQuery(id+"F17.opExtrude","CAP_FACE",FACE,{"disambiguationData":[OSD([sQuery(id+"F16.wireOp",EDGE,"E21")])],"isStart":false});var subQ1=makeQuery(id+"F20.opExtrude","SWEPT_FACE",FACE,{"disambiguationData":[OSD([sQuery(id+"F19.wireOp",EDGE,"E72")])]});Q16=makeQuery(id+"F21.boolean.opBoolean","SPLIT",EDGE,{"disambiguationData":[TD([makeQuery(id+"F21.opExtrude","SWEPT_FACE",FACE,{"disambiguationData":[OSD([sQuery(id+"F18.wireOp",EDGE,"30cf533b-c859-4f95-b794-18c5afbc5071.3.0")])]})])],"derivedFrom":makeQuery(id+"F20.boolean.opBoolean","INTERSECT",EDGE,{"derivedFrom":[subQ0,subQ1]})});}
            var Q17;
            {var subQ0=makeQuery(id+"F17.opExtrude","CAP_FACE",FACE,{"disambiguationData":[OSD([sQuery(id+"F16.wireOp",EDGE,"E21")])],"isStart":false});var subQ1=makeQuery(id+"F20.opExtrude","SWEPT_FACE",FACE,{"disambiguationData":[OSD([sQuery(id+"F19.wireOp",EDGE,"E72")])]});Q17=makeQuery(id+"F21.boolean.opBoolean","SPLIT",EDGE,{"disambiguationData":[TD([makeQuery(id+"F21.opExtrude","SWEPT_FACE",FACE,{"disambiguationData":[OSD([sQuery(id+"F18.wireOp",EDGE,"30cf533b-c859-4f95-b794-18c5afbc5071.1.0")])]})])],"derivedFrom":makeQuery(id+"F20.boolean.opBoolean","INTERSECT",EDGE,{"derivedFrom":[subQ0,subQ1]})});}
            var Q18;
            {var subQ0=makeQuery(id+"F17.opExtrude","CAP_FACE",FACE,{"disambiguationData":[OSD([sQuery(id+"F16.wireOp",EDGE,"E21")])],"isStart":false});var subQ1=makeQuery(id+"F20.opExtrude","SWEPT_FACE",FACE,{"disambiguationData":[OSD([sQuery(id+"F19.wireOp",EDGE,"E72")])]});Q18=makeQuery(id+"F21.boolean.opBoolean","SPLIT",EDGE,{"disambiguationData":[TD([makeQuery(id+"F21.opExtrude","SWEPT_FACE",FACE,{"disambiguationData":[OSD([sQuery(id+"F18.wireOp",EDGE,"emLC8hOE-DqrB-nXh3-jQE7-6hVRjXGIrFug")])]})])],"derivedFrom":makeQuery(id+"F20.boolean.opBoolean","INTERSECT",EDGE,{"derivedFrom":[subQ0,subQ1]})});}
            var Q19;
            {var subQ0=makeQuery(id+"F17.opExtrude","CAP_FACE",FACE,{"disambiguationData":[OSD([sQuery(id+"F16.wireOp",EDGE,"E21")])],"isStart":false});var subQ1=makeQuery(id+"F20.opExtrude","SWEPT_FACE",FACE,{"disambiguationData":[OSD([sQuery(id+"F19.wireOp",EDGE,"E72")])]});Q19=makeQuery(id+"F21.boolean.opBoolean","SPLIT",EDGE,{"disambiguationData":[TD([makeQuery(id+"F21.opExtrude","SWEPT_FACE",FACE,{"disambiguationData":[OSD([sQuery(id+"F18.wireOp",EDGE,"30cf533b-c859-4f95-b794-18c5afbc5071.45.0")])]})])],"derivedFrom":makeQuery(id+"F20.boolean.opBoolean","INTERSECT",EDGE,{"derivedFrom":[subQ0,subQ1]})});}
            var Q20;
            {var subQ0=makeQuery(id+"F17.opExtrude","CAP_FACE",FACE,{"disambiguationData":[OSD([sQuery(id+"F16.wireOp",EDGE,"E21")])],"isStart":false});var subQ1=makeQuery(id+"F20.opExtrude","SWEPT_FACE",FACE,{"disambiguationData":[OSD([sQuery(id+"F19.wireOp",EDGE,"E72")])]});Q20=makeQuery(id+"F21.boolean.opBoolean","SPLIT",EDGE,{"disambiguationData":[TD([makeQuery(id+"F21.opExtrude","SWEPT_FACE",FACE,{"disambiguationData":[OSD([sQuery(id+"F18.wireOp",EDGE,"30cf533b-c859-4f95-b794-18c5afbc5071.43.0")])]})])],"derivedFrom":makeQuery(id+"F20.boolean.opBoolean","INTERSECT",EDGE,{"derivedFrom":[subQ0,subQ1]})});}
            var Q21;
            {var subQ0=makeQuery(id+"F17.opExtrude","CAP_FACE",FACE,{"disambiguationData":[OSD([sQuery(id+"F16.wireOp",EDGE,"E21")])],"isStart":false});var subQ1=makeQuery(id+"F20.opExtrude","SWEPT_FACE",FACE,{"disambiguationData":[OSD([sQuery(id+"F19.wireOp",EDGE,"E72")])]});Q21=makeQuery(id+"F21.boolean.opBoolean","SPLIT",EDGE,{"disambiguationData":[TD([makeQuery(id+"F21.opExtrude","SWEPT_FACE",FACE,{"disambiguationData":[OSD([sQuery(id+"F18.wireOp",EDGE,"30cf533b-c859-4f95-b794-18c5afbc5071.7.0")])]})])],"derivedFrom":makeQuery(id+"F20.boolean.opBoolean","INTERSECT",EDGE,{"derivedFrom":[subQ0,subQ1]})});}
            var Q22;
            {var subQ0=makeQuery(id+"F17.opExtrude","CAP_FACE",FACE,{"disambiguationData":[OSD([sQuery(id+"F16.wireOp",EDGE,"E21")])],"isStart":false});var subQ1=makeQuery(id+"F20.opExtrude","SWEPT_FACE",FACE,{"disambiguationData":[OSD([sQuery(id+"F19.wireOp",EDGE,"E72")])]});Q22=makeQuery(id+"F21.boolean.opBoolean","SPLIT",EDGE,{"disambiguationData":[TD([makeQuery(id+"F21.opExtrude","SWEPT_FACE",FACE,{"disambiguationData":[OSD([sQuery(id+"F18.wireOp",EDGE,"30cf533b-c859-4f95-b794-18c5afbc5071.9.0")])]})])],"derivedFrom":makeQuery(id+"F20.boolean.opBoolean","INTERSECT",EDGE,{"derivedFrom":[subQ0,subQ1]})});}
            var Q23;
            {var subQ0=makeQuery(id+"F17.opExtrude","CAP_FACE",FACE,{"disambiguationData":[OSD([sQuery(id+"F16.wireOp",EDGE,"E21")])],"isStart":false});var subQ1=makeQuery(id+"F20.opExtrude","SWEPT_FACE",FACE,{"disambiguationData":[OSD([sQuery(id+"F19.wireOp",EDGE,"E72")])]});Q23=makeQuery(id+"F21.boolean.opBoolean","SPLIT",EDGE,{"disambiguationData":[TD([makeQuery(id+"F21.opExtrude","SWEPT_FACE",FACE,{"disambiguationData":[OSD([sQuery(id+"F18.wireOp",EDGE,"30cf533b-c859-4f95-b794-18c5afbc5071.11.0")])]})])],"derivedFrom":makeQuery(id+"F20.boolean.opBoolean","INTERSECT",EDGE,{"derivedFrom":[subQ0,subQ1]})});}
            var Q24;
            {var subQ0=makeQuery(id+"F17.opExtrude","CAP_FACE",FACE,{"disambiguationData":[OSD([sQuery(id+"F16.wireOp",EDGE,"E21")])],"isStart":false});var subQ1=makeQuery(id+"F20.opExtrude","SWEPT_FACE",FACE,{"disambiguationData":[OSD([sQuery(id+"F19.wireOp",EDGE,"E72")])]});Q24=makeQuery(id+"F21.boolean.opBoolean","SPLIT",EDGE,{"disambiguationData":[TD([makeQuery(id+"F21.opExtrude","SWEPT_FACE",FACE,{"disambiguationData":[OSD([sQuery(id+"F18.wireOp",EDGE,"30cf533b-c859-4f95-b794-18c5afbc5071.13.0")])]})])],"derivedFrom":makeQuery(id+"F20.boolean.opBoolean","INTERSECT",EDGE,{"derivedFrom":[subQ0,subQ1]})});}
            var Q25;
            {var subQ0=makeQuery(id+"F17.opExtrude","CAP_FACE",FACE,{"disambiguationData":[OSD([sQuery(id+"F16.wireOp",EDGE,"E21")])],"isStart":false});var subQ1=makeQuery(id+"F20.opExtrude","SWEPT_FACE",FACE,{"disambiguationData":[OSD([sQuery(id+"F19.wireOp",EDGE,"E72")])]});Q25=makeQuery(id+"F21.boolean.opBoolean","SPLIT",EDGE,{"disambiguationData":[TD([makeQuery(id+"F21.opExtrude","SWEPT_FACE",FACE,{"disambiguationData":[OSD([sQuery(id+"F18.wireOp",EDGE,"30cf533b-c859-4f95-b794-18c5afbc5071.15.0")])]})])],"derivedFrom":makeQuery(id+"F20.boolean.opBoolean","INTERSECT",EDGE,{"derivedFrom":[subQ0,subQ1]})});}
            var Q26;
            {var subQ0=makeQuery(id+"F17.opExtrude","CAP_FACE",FACE,{"disambiguationData":[OSD([sQuery(id+"F16.wireOp",EDGE,"E21")])],"isStart":false});var subQ1=makeQuery(id+"F20.opExtrude","SWEPT_FACE",FACE,{"disambiguationData":[OSD([sQuery(id+"F19.wireOp",EDGE,"E72")])]});Q26=makeQuery(id+"F21.boolean.opBoolean","SPLIT",EDGE,{"disambiguationData":[TD([makeQuery(id+"F21.opExtrude","SWEPT_FACE",FACE,{"disambiguationData":[OSD([sQuery(id+"F18.wireOp",EDGE,"30cf533b-c859-4f95-b794-18c5afbc5071.41.0")])]})])],"derivedFrom":makeQuery(id+"F20.boolean.opBoolean","INTERSECT",EDGE,{"derivedFrom":[subQ0,subQ1]})});}
            var Q27;
            {var subQ0=makeQuery(id+"F17.opExtrude","CAP_FACE",FACE,{"disambiguationData":[OSD([sQuery(id+"F16.wireOp",EDGE,"E21")])],"isStart":false});var subQ1=makeQuery(id+"F20.opExtrude","SWEPT_FACE",FACE,{"disambiguationData":[OSD([sQuery(id+"F19.wireOp",EDGE,"E72")])]});Q27=makeQuery(id+"F21.boolean.opBoolean","SPLIT",EDGE,{"disambiguationData":[TD([makeQuery(id+"F21.opExtrude","SWEPT_FACE",FACE,{"disambiguationData":[OSD([sQuery(id+"F18.wireOp",EDGE,"30cf533b-c859-4f95-b794-18c5afbc5071.39.0")])]})])],"derivedFrom":makeQuery(id+"F20.boolean.opBoolean","INTERSECT",EDGE,{"derivedFrom":[subQ0,subQ1]})});}
            var Q28;
            Q28=makeQuery(id+"F17.opExtrude","CAP_EDGE",EDGE,{"disambiguationData":[OSD([sQuery(id+"F16.wireOp",EDGE,"E21")])],"isStart":true});
            fillet(context, id + "F35", {"entities" : qUnion([Q0, Q1, Q2, Q3, Q4, Q5, Q6, Q7, Q8, Q9, Q10, Q11, Q12, Q13, Q14, Q15, Q16, Q17, Q18, Q19, Q20, Q21, Q22, Q23, Q24, Q25, Q26, Q27, Q28]), "radius" : .5 * mm, "tangentPropagation" : true, "allowEdgeOverflow" : false});
        }
    });
